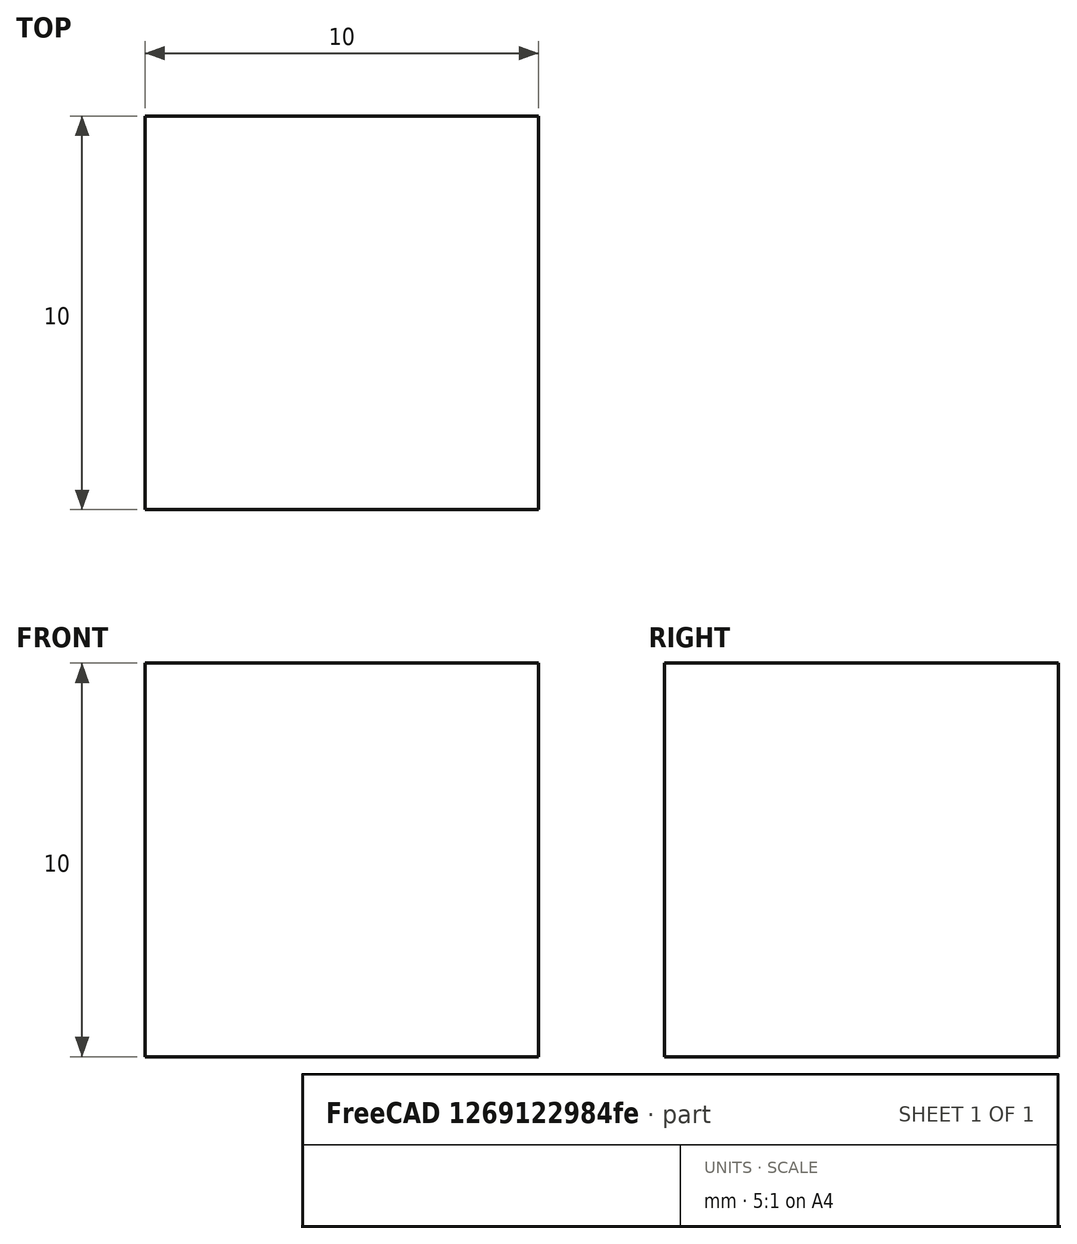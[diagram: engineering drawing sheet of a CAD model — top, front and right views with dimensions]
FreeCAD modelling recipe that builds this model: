
FCSTD DOCUMENT  (FreeCAD 0.21R33694 (Git))
Label: OJT1_T11P01_migcercledecubs
License: All rights reserved
LicenseURL: http://en.wikipedia.org/wiki/All_rights_reserved
objects: Part::Box×1, Part::FeaturePython×1
note: 1 computed .brp shape members not serialized (recipe doc carries the construction recipe); baked Part::Feature solids carry a one-line shape summary decoded from their .brp

FEATURE [Part::Box] Box  label="Cube"
  AttacherType = Attacher::AttachEngine3D
  Height = 10
  Length = 10
  Placement = pos=(9,-5,0) rot=(0,0,1;0rad)
  Width = 10
FEATURE [Part::FeaturePython] Array  # Draft array (typed FeaturePython)
  AlwaysSyncPlacement = false
  Angle = 180
  ArrayType = 1
  Axis = (0,0,1)
  Base = -> Box
  Center = (-6.52,-1.8,0)
  Count = 5
  ExpandArray = false
  Fuse = false
  IntervalAxis = (0,0,0)
  IntervalX = (50,0,0)
  IntervalY = (0,50,0)
  IntervalZ = (0,0,50)
  NumberCircles = 3
  NumberPolar = 5
  NumberX = 2
  NumberY = 2
  NumberZ = 1
  Placement = pos=(7,1,0) rot=(0,0,1;0rad)
  PlacementList = 5 placements: [(9,-5,0),(6.71704,6.91156,0),(-3.32,13.72,0),(-15.2316,11.437,0),(-22.04,1.4,0)]
  RadialDistance = 50
  ScaleList = (5) [(1,1,1),(1,1,1),(1,1,1),(1,1,1),(1,1,1)]
  Symmetry = 1
  TangentialDistance = 25
